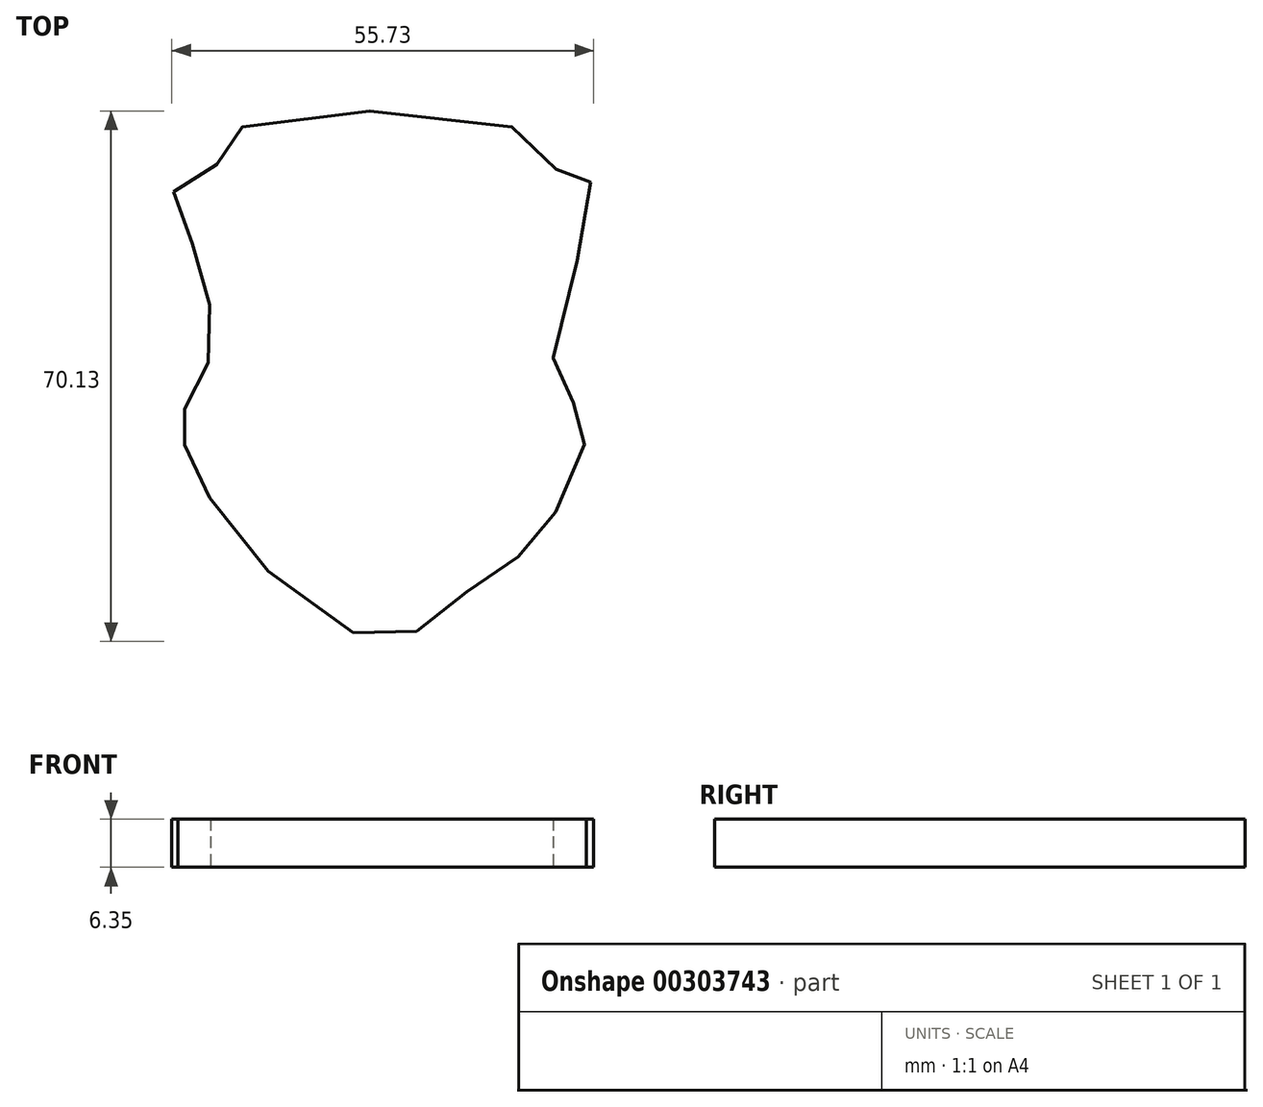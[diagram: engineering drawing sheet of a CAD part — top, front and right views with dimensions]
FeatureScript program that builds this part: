
annotation { "Feature Type Name" : "Feature", "Feature Type Description" : "" }
export const myFeature = defineFeature(function(context is Context, id is Id, definition is map)
    precondition{}
    {
        {
            var Q0;
            Q0=qCreatedBy(makeId("Top.planeOp"),FACE);
            var sketch = newSketch(context, id + "F0", { "sketchPlane" : qUnion([Q0])});
            skLineSegment(sketch, "E0.bottom", {"start": v(-39.92, 32.16) * mm, "end": v(34.78, 32.16) * mm});
            skLineSegment(sketch, "E0.top", {"start": v(-39.92, -42.2) * mm, "end": v(34.78, -42.2) * mm});
            skLineSegment(sketch, "E0.left", {"start": v(-39.92, 32.16) * mm, "end": v(-39.92, -42.2) * mm});
            skLineSegment(sketch, "E0.right", {"start": v(34.78, 32.16) * mm, "end": v(34.78, -42.2) * mm});
            skSolve(sketch);
        }
        {
            var Q0;
            Q0=qCreatedBy(makeId("Top.planeOp"),FACE);
            var sketch = newSketch(context, id + "F1", { "sketchPlane" : qUnion([Q0])});
            skFitSpline(sketch, "E1", {"points": [v(-32.61, 20.27) * mm, v(-29.57, 12.34) * mm, v(-27.74, 2.6) * mm, v(-28.96, -5.33) * mm, v(-32, -10.21) * mm, v(-30.78, -13.87) * mm, v(-25, -24.54) * mm, v(-4.88, -39.17) * mm, v(3.05, -34.9) * mm, v(11.89, -28.8) * mm, v(17.68, -22.4) * mm, v(21.95, -10.82) * mm, v(19.81, -7.16) * mm, v(17.68, 0) * mm, v(22.56, 21.49) * mm, v(18.6, 22.4) * mm, v(15.54, 27.28) * mm, v(-24.69, 28.2) * mm, v(-26.82, 23.93) * mm, v(-32.61, 20.27) * mm]});
            skSolve(sketch);
        }
        {
            var Q0;
            Q0 = qSketchRegion(id + "F1", true);
            extrude(context, id + "F2", {"entities" : qUnion([Q0]), "depth" : 6.35 * mm});
        }
    });
